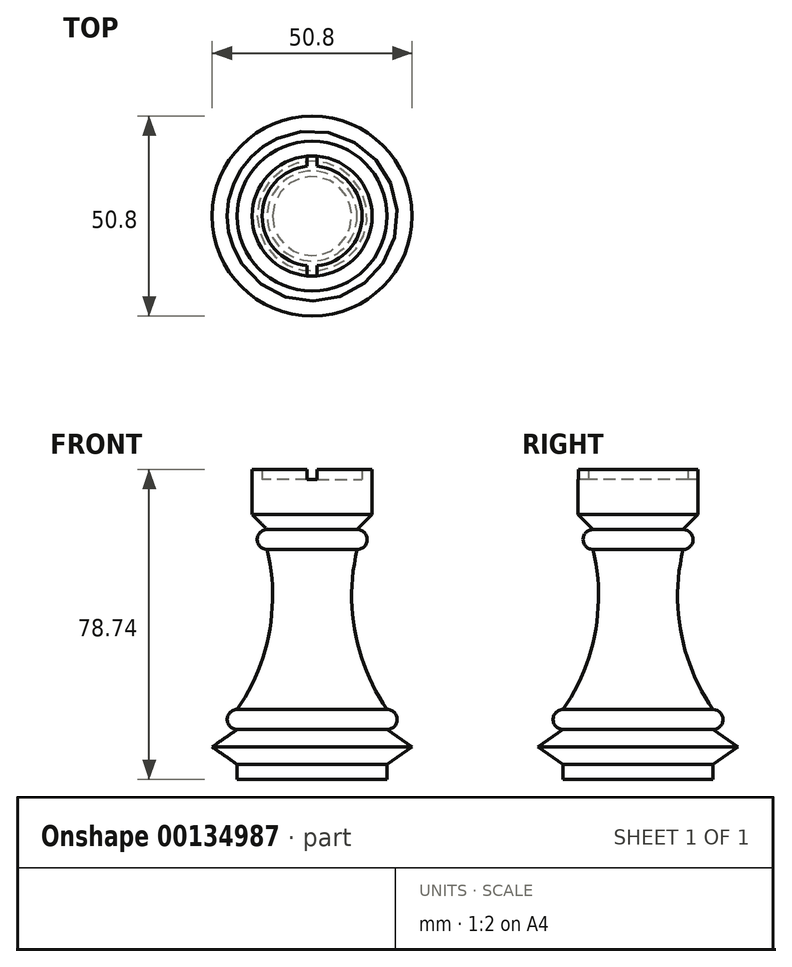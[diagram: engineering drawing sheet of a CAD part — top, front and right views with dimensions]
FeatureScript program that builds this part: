
annotation { "Feature Type Name" : "Feature", "Feature Type Description" : "" }
export const myFeature = defineFeature(function(context is Context, id is Id, definition is map)
    precondition{}
    {
        {
            var Q0;
            Q0=qCreatedBy(makeId("Front.planeOp"),FACE);
            var sketch = newSketch(context, id + "F0", { "sketchPlane" : qUnion([Q0])});
            skLineSegment(sketch, "E0", {"start": v(0, 0) * mm, "end": v(19.05, 0) * mm});
            skLineSegment(sketch, "E1", {"start": v(19.05, 0) * mm, "end": v(19.05, 3.81) * mm});
            skLineSegment(sketch, "E2", {"start": v(19.05, 3.8) * mm, "end": v(25.4, 8.26) * mm});
            skLineSegment(sketch, "E3", {"start": v(25.4, 8.26) * mm, "end": v(19.05, 12.7) * mm});
            skLineSegment(sketch, "E4", {"start": v(0, 0) * mm, "end": v(0, 76.2) * mm});
            skLineSegment(sketch, "E5", {"start": v(0, 76.2) * mm, "end": v(12.7, 76.2) * mm});
            skLineSegment(sketch, "E6", {"start": v(12.7, 76.2) * mm, "end": v(12.7, 78.74) * mm});
            skLineSegment(sketch, "E7", {"start": v(12.7, 78.74) * mm, "end": v(15.24, 78.74) * mm});
            skLineSegment(sketch, "E8", {"start": v(15.24, 78.74) * mm, "end": v(15.24, 67.31) * mm});
            skLineSegment(sketch, "E9", {"start": v(15.24, 67.31) * mm, "end": v(11.43, 63.5) * mm});
            skArc(sketch, "E10", {"start": v(11.43, 58.42) * mm, "mid": v(13.97, 60.96) * mm, "end": v(11.43, 63.5) * mm});
            skArc(sketch, "E11", {"start": v(19.05, 12.7) * mm, "mid": v(21.6, 15.24) * mm, "end": v(19.05, 17.78) * mm});
            skArc(sketch, "E12", {"start": v(11.43, 58.42) * mm, "mid": v(10.92, 37.29) * mm, "end": v(19.05, 17.78) * mm});
            skSolve(sketch);
        }
        {
            var Q0;
            Q0=makeQuery(id+"F0.imprint","IMPRINT",FACE,{"disambiguationData":[TD([[makeQuery(id+"F0.imprint","IMPRINT",EDGE,{"derivedFrom":sQuery(id+"F0.wireOp",EDGE,"E0")}),1.0]])]});
            var Q1;
            Q1=sQuery(id+"F0.wireOp",EDGE,"E4");
            revolve(context, id + "F1", {"entities" : qUnion([Q0]), "axis" : qUnion([Q1]), "revolveType" : RevolveType.FULL});
        }
        {
            var Q0;
            Q0=qCreatedBy(makeId("Front.planeOp"),FACE);
            var sketch = newSketch(context, id + "F2", { "sketchPlane" : qUnion([Q0])});
            skLineSegment(sketch, "E13.bottom", {"start": v(1.27, 78.74) * mm, "end": v(-1.27, 78.74) * mm});
            skLineSegment(sketch, "E13.top", {"start": v(1.27, 76.2) * mm, "end": v(-1.27, 76.2) * mm});
            skLineSegment(sketch, "E13.left", {"start": v(1.27, 78.74) * mm, "end": v(1.27, 76.2) * mm});
            skLineSegment(sketch, "E13.right", {"start": v(-1.27, 78.74) * mm, "end": v(-1.27, 76.2) * mm});
            skPoint(sketch, "E13.middle", {"position": v(0, 77.47) * mm});
            skSolve(sketch);
        }
        {
            var Q0;
            Q0 = qSketchRegion(id + "F2", true);
            extrude(context, id + "F3", {"entities" : qUnion([Q0]), "operationType" : NewBodyOperationType.REMOVE, "endBound" : BoundingType.THROUGH_ALL, "oppositeDirection" : true, "depth" : 25.4 * mm, "hasSecondDirection" : true, "secondDirectionOppositeDirection" : false, "secondDirectionDepth" : 25.4 * mm});
        }
    });
